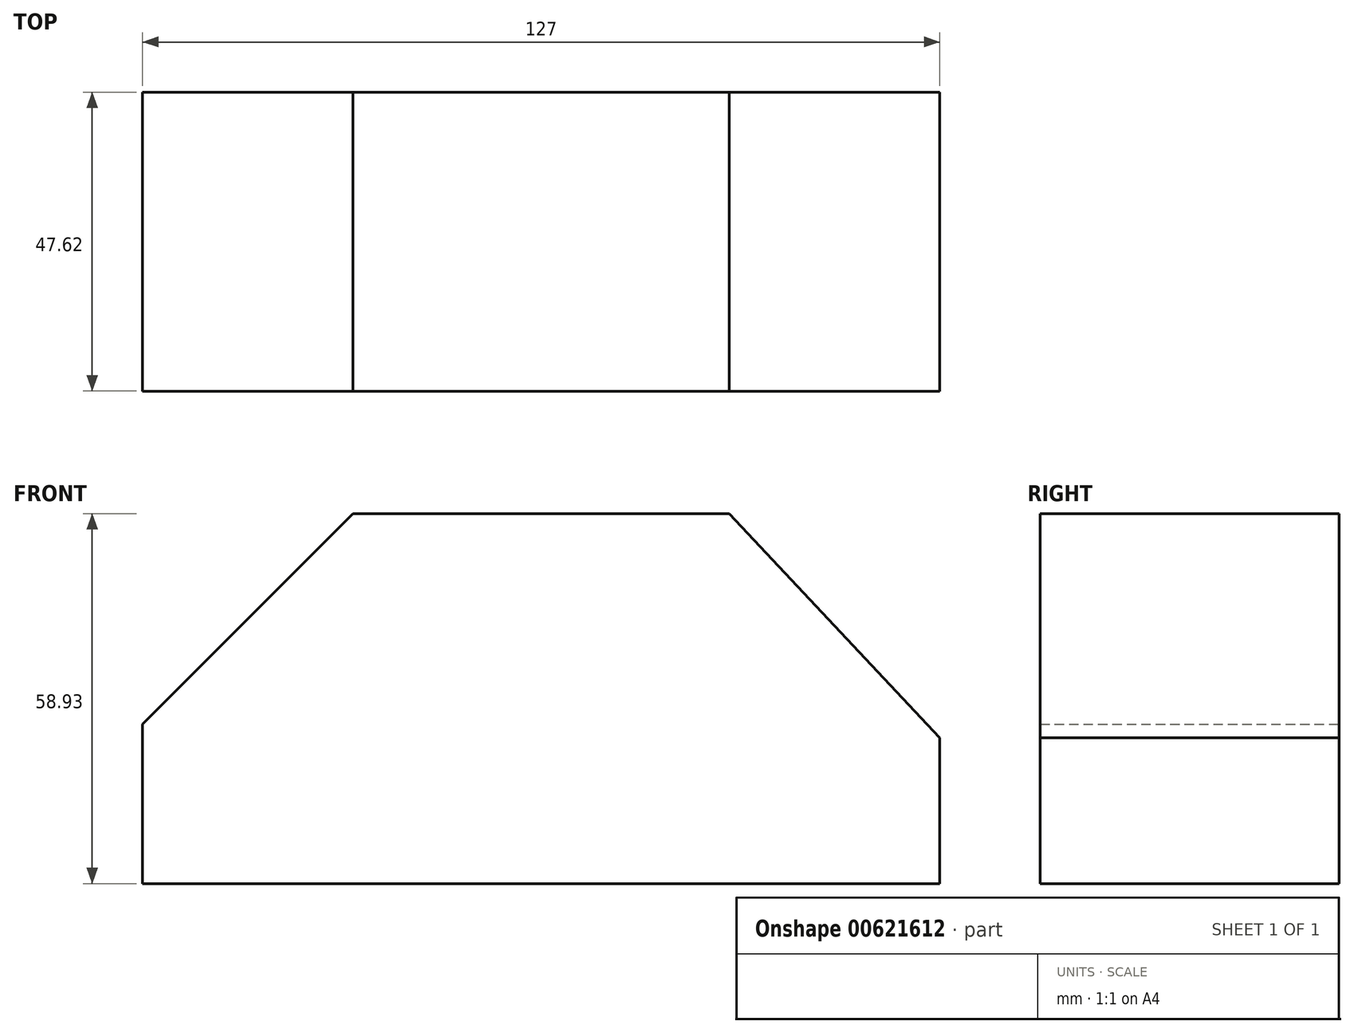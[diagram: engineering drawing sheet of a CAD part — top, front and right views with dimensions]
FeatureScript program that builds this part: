
annotation { "Feature Type Name" : "Feature", "Feature Type Description" : "" }
export const myFeature = defineFeature(function(context is Context, id is Id, definition is map)
    precondition{}
    {
        {
            var Q0;
            Q0=qCreatedBy(makeId("Front.planeOp"),FACE);
            var sketch = newSketch(context, id + "F0", { "sketchPlane" : qUnion([Q0])});
            skLineSegment(sketch, "E0", {"start": v(-67.95, 0) * mm, "end": v(59.05, 0) * mm});
            skLineSegment(sketch, "E1", {"start": v(59.05, 0) * mm, "end": v(59.05, 58.93) * mm, "construction": true});
            skLineSegment(sketch, "E2", {"start": v(59.05, 58.93) * mm, "end": v(-67.95, 58.93) * mm, "construction": true});
            skLineSegment(sketch, "E3", {"start": v(-67.95, 58.93) * mm, "end": v(-67.95, 0) * mm, "construction": true});
            skLineSegment(sketch, "E4", {"start": v(-67.95, 0) * mm, "end": v(-67.95, 25.4) * mm});
            skLineSegment(sketch, "E5", {"start": v(-67.95, 58.93) * mm, "end": v(-34.42, 58.93) * mm, "construction": true});
            skLineSegment(sketch, "E6", {"start": v(-67.95, 25.4) * mm, "end": v(-34.42, 58.93) * mm});
            skLineSegment(sketch, "E7", {"start": v(59.05, 0) * mm, "end": v(59.05, 23.2) * mm});
            skLineSegment(sketch, "E8", {"start": v(59.05, 58.93) * mm, "end": v(25.52, 58.93) * mm, "construction": true});
            skLineSegment(sketch, "E9", {"start": v(25.52, 58.93) * mm, "end": v(59.05, 23.2) * mm});
            skLineSegment(sketch, "E10", {"start": v(25.52, 58.93) * mm, "end": v(-34.42, 58.93) * mm});
            skSolve(sketch);
        }
        {
            var Q0;
            Q0=makeQuery(id+"F0.imprint","IMPRINT",FACE,{"disambiguationData":[TD([[makeQuery(id+"F0.imprint","IMPRINT",EDGE,{"derivedFrom":sQuery(id+"F0.wireOp",EDGE,"E0")}),1.0]])]});
            extrude(context, id + "F1", {"entities" : qUnion([Q0]), "depth" : 47.62 * mm, "offsetDistance" : 25.4 * mm});
        }
    });
